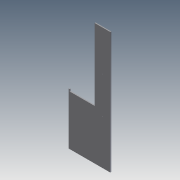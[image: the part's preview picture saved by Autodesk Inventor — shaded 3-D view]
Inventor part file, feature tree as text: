
AUTODESK INVENTOR PART (.ipt)
format: ipt  version: 2011 (Build 150239000, 239)  size: 174,592 bytes
history: native  units: in
note: dims shown in document units (in); Inventor stores cm internally (conversion verified against a paired STEP export)
features: extrude x13, sketch x13
ambient origin geometry x8: Origin, YZ Plane, XZ Plane, XY Plane, X Axis, Y Axis, Z Axis, Center Point
bodies: Solid1 (feature_tree)
feature tree (26):
  extrude  "Extrusion1"  Depth=35.0in
  extrude  "Extrusion2"  Depth=18.14in
  extrude  "Extrusion3"  Depth=0.25in TaperAngle=0.0deg
  extrude  "Extrusion4"  Depth=0.25in TaperAngle=0.0deg
  extrude  "Extrusion5"  Depth=0.25in TaperAngle=0.0deg
  extrude  "Extrusion6"  Depth=12.75in
  extrude  "Extrusion7"  Depth=0.5in
  extrude  "Extrusion8"  Depth=0.25in
  extrude  "Extrusion9"  Depth=0.25in TaperAngle=0.0deg
  extrude  "Extrusion10"  Depth=0.25in TaperAngle=0.0deg
  extrude  "Extrusion11"  Depth=0.185in
  extrude  "Extrusion12"  Depth=9.075in
  extrude  "Extrusion13"  Depth=0.5in
  sketch  "Sketch1"  dims[d0=10.0in d1=35.0in]
  sketch  "Sketch2"  dims[d2=6.0in d3=18.14in]
  sketch  "Sketch3"  dims[d4=0.25in d5=0.0in d6=0.25in d7=0.0in]
  sketch  "Sketch4"  dims[d8=0.125in d9=0.25in d10=0.0in]
  sketch  "Sketch5"  dims[d11=0.25in d12=0.0in d13=0.25in d14=0.0in]
  sketch  "Sketch6"  dims[d15=0.25in d16=0.0in d17=12.75in]
  sketch  "Sketch7"  dims[d18=1.0in d19=0.0in d20=0.5in]
  sketch  "Sketch8"  dims[d21=1.0in d22=0.0in d23=0.25in]
  sketch  "Sketch9"  dims[d24=0.5in d25=0.25in d26=0.0in]
  sketch  "Sketch10"  dims[d27=0.75in d28=0.25in d29=0.0in]
  sketch  "Sketch11"  dims[d30=20.0in d31=0.185in]
  sketch  "Sketch12"  dims[d32=1.0in d33=0.0in d34=9.075in]
  sketch  "Sketch13"  dims[d35=1.0in d36=0.0in d37=0.5in d38=1.0in d39=0.0in]
